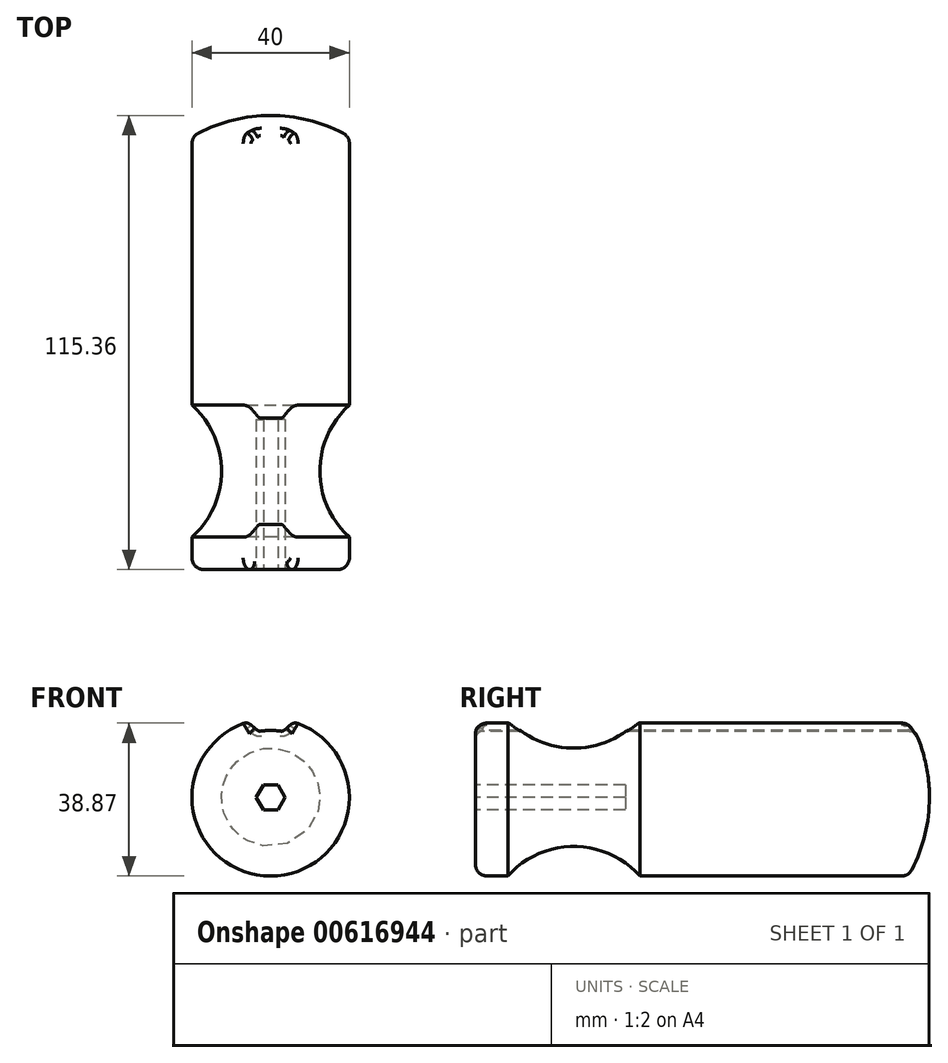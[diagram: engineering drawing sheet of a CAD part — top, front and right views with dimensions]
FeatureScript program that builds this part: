
annotation { "Feature Type Name" : "Feature", "Feature Type Description" : "" }
export const myFeature = defineFeature(function(context is Context, id is Id, definition is map)
    precondition{}
    {
        {
            var Q0;
            Q0=qCreatedBy(makeId("Right.planeOp"),FACE);
            var sketch = newSketch(context, id + "F0", { "sketchPlane" : qUnion([Q0])});
            skLineSegment(sketch, "E0", {"start": v(0, 0) * mm, "end": v(184.97, 0) * mm, "construction": true});
            skLineSegment(sketch, "E1", {"start": v(0, 0) * mm, "end": v(0, 20) * mm});
            skLineSegment(sketch, "E2", {"start": v(0, 20) * mm, "end": v(110, 20) * mm});
            skArc(sketch, "E3", {"start": v(115.36, 0) * mm, "mid": v(114, 10.35) * mm, "end": v(110, 20) * mm});
            skLineSegment(sketch, "E4", {"start": v(0, 0) * mm, "end": v(115.36, 0) * mm});
            skSolve(sketch);
        }
        {
            var Q0;
            Q0=makeQuery(id+"F0.imprint","IMPRINT",FACE,{"disambiguationData":[TD([[makeQuery(id+"F0.imprint","IMPRINT",EDGE,{"derivedFrom":sQuery(id+"F0.wireOp",EDGE,"E1")}),-1.0]])]});
            var Q1;
            Q1=sQuery(id+"F0.wireOp",EDGE,"E4");
            revolve(context, id + "F1", {"entities" : qUnion([Q0]), "axis" : qUnion([Q1]), "revolveType" : RevolveType.FULL});
        }
        {
            var Q0;
            Q0=makeQuery(id+"F1.opRevolve","SWEPT_EDGE",EDGE,{"disambiguationData":[OSD([sQuery(id+"F0.wireOp",EDGE,"E1"),sQuery(id+"F0.wireOp",EDGE,"E2")])]});
            var Q1;
            Q1=makeQuery(id+"F1.opRevolve","SWEPT_EDGE",EDGE,{"disambiguationData":[OSD([sQuery(id+"F0.wireOp",EDGE,"E2"),sQuery(id+"F0.wireOp",EDGE,"E3")])]});
            fillet(context, id + "F2", {"entities" : qUnion([Q0, Q1]), "radius" : 3 * mm, "tangentPropagation" : true, "allowEdgeOverflow" : false});
        }
        {
            var Q0;
            Q0=makeQuery(id+"F1.opRevolve","SWEPT_FACE",FACE,{"disambiguationData":[OSD([sQuery(id+"F0.wireOp",EDGE,"E1")])]});
            var sketch = newSketch(context, id + "F3", { "sketchPlane" : qUnion([Q0])});
            skCircle(sketch, "E5.0", {"center": v(0, 0) * mm, "radius": 17 * mm});
            skLineSegment(sketch, "E6", {"start": v(3, 16.73) * mm, "end": v(13, 25.12) * mm});
            skLineSegment(sketch, "E7", {"start": v(-3, 16.73) * mm, "end": v(-13, 25.12) * mm});
            skLineSegment(sketch, "E8", {"start": v(-13, 25.12) * mm, "end": v(13, 25.12) * mm});
            skLineSegment(sketch, "E9", {"start": v(0, 0) * mm, "end": v(0, 47.12) * mm, "construction": true});
            skPoint(sketch, "E10", {"position": v(0, 25.12) * mm});
            skSolve(sketch);
        }
        {
            var Q0;
            {var subQ0=sQuery(id+"F3.wireOp",EDGE,"E6");Q0=makeQuery(id+"F3.imprint","IMPRINT",FACE,{"disambiguationData":[TD([[makeQuery(id+"F3.imprint","IMPRINT",EDGE,{"derivedFrom":subQ0}),1.0]])]});}
            extrude(context, id + "F4", {"entities" : qUnion([Q0]), "operationType" : NewBodyOperationType.REMOVE, "endBound" : BoundingType.THROUGH_ALL, "oppositeDirection" : true, "depth" : 25 * mm, "offsetDistance" : 25 * mm});
        }
        {
            var Q0;
            Q0=makeQuery(id+"F4.boolean.opBoolean","COPY",EDGE,{"derivedFrom":makeQuery(id+"F4.opExtrude","SWEPT_EDGE",EDGE,{"disambiguationData":[OSD([sQuery(id+"F3.wireOp",EDGE,"E5.0"),sQuery(id+"F3.wireOp",EDGE,"E7")])]})});
            var Q1;
            Q1=makeQuery(id+"F4.boolean.opBoolean","COPY",EDGE,{"derivedFrom":makeQuery(id+"F4.opExtrude","SWEPT_EDGE",EDGE,{"disambiguationData":[OSD([sQuery(id+"F3.wireOp",EDGE,"E5.0"),sQuery(id+"F3.wireOp",EDGE,"E6")])]})});
            fillet(context, id + "F5", {"entities" : qUnion([Q0, Q1]), "radius" : 1 * mm, "tangentPropagation" : true, "allowEdgeOverflow" : false});
        }
        {
            var Q0;
            Q0=makeQuery(id+"F4.boolean.opBoolean","INTERSECT",EDGE,{"derivedFrom":[makeQuery(id+"F1.opRevolve","SWEPT_FACE",FACE,{"disambiguationData":[OSD([sQuery(id+"F0.wireOp",EDGE,"E2")])]}),makeQuery(id+"F4.opExtrude","SWEPT_FACE",FACE,{"disambiguationData":[OSD([sQuery(id+"F3.wireOp",EDGE,"E7")])]})]});
            var Q1;
            Q1=makeQuery(id+"F4.boolean.opBoolean","INTERSECT",EDGE,{"derivedFrom":[makeQuery(id+"F1.opRevolve","SWEPT_FACE",FACE,{"disambiguationData":[OSD([sQuery(id+"F0.wireOp",EDGE,"E2")])]}),makeQuery(id+"F4.opExtrude","SWEPT_FACE",FACE,{"disambiguationData":[OSD([sQuery(id+"F3.wireOp",EDGE,"E6")])]})]});
            fillet(context, id + "F6", {"entities" : qUnion([Q0, Q1]), "radius" : 2 * mm, "tangentPropagation" : true, "allowEdgeOverflow" : false});
        }
        {
            var Q0;
            Q0=qCreatedBy(makeId("Right.planeOp"),FACE);
            var sketch = newSketch(context, id + "F7", { "sketchPlane" : qUnion([Q0])});
            skCircle(sketch, "E11", {"center": v(25, 35) * mm, "radius": 22.5 * mm});
            skSolve(sketch);
        }
        {
            var Q0;
            Q0=makeQuery(id+"F7.imprint","IMPRINT",FACE,{"disambiguationData":[TD([[makeQuery(id+"F7.imprint","IMPRINT",EDGE,{"derivedFrom":sQuery(id+"F7.wireOp",EDGE,"E11")}),1.0]])]});
            var Q1;
            Q1=sQuery(id+"F0.wireOp",EDGE,"E0");
            revolve(context, id + "F8", {"operationType" : NewBodyOperationType.REMOVE, "entities" : qUnion([Q0]), "axis" : qUnion([Q1]), "revolveType" : RevolveType.FULL, "oppositeDirection" : true});
        }
        {
            var Q0;
            Q0=makeQuery(id+"F1.opRevolve","SWEPT_FACE",FACE,{"disambiguationData":[OSD([sQuery(id+"F0.wireOp",EDGE,"E1")])]});
            var sketch = newSketch(context, id + "F9", { "sketchPlane" : qUnion([Q0])});
            skCircle(sketch, "E12.cCircle", {"center": v(0, 0) * mm, "radius": 3.17 * mm, "construction": true});
            skLineSegment(sketch, "E12.0", {"start": v(1.83, -3.17) * mm, "end": v(-1.83, -3.17) * mm});
            skLineSegment(sketch, "E12.1", {"start": v(-1.83, -3.17) * mm, "end": v(-3.67, 0) * mm});
            skLineSegment(sketch, "E12.2", {"start": v(-3.67, 0) * mm, "end": v(-1.83, 3.17) * mm});
            skLineSegment(sketch, "E12.3", {"start": v(-1.83, 3.17) * mm, "end": v(1.83, 3.18) * mm});
            skLineSegment(sketch, "E12.4", {"start": v(1.83, 3.18) * mm, "end": v(3.67, 0) * mm});
            skLineSegment(sketch, "E12.5", {"start": v(3.67, 0) * mm, "end": v(1.83, -3.17) * mm});
            skPoint(sketch, "E12.0.midPoint", {"position": v(0, -3.17) * mm});
            skSolve(sketch);
        }
        {
            var Q0;
            Q0=makeQuery(id+"F9.imprint","IMPRINT",FACE,{"disambiguationData":[TD([[makeQuery(id+"F9.imprint","IMPRINT",EDGE,{"derivedFrom":sQuery(id+"F9.wireOp",EDGE,"E12.0")}),-1.0]])]});
            extrude(context, id + "F10", {"entities" : qUnion([Q0]), "operationType" : NewBodyOperationType.REMOVE, "oppositeDirection" : true, "depth" : 38.1 * mm, "offsetDistance" : 25 * mm});
        }
    });
